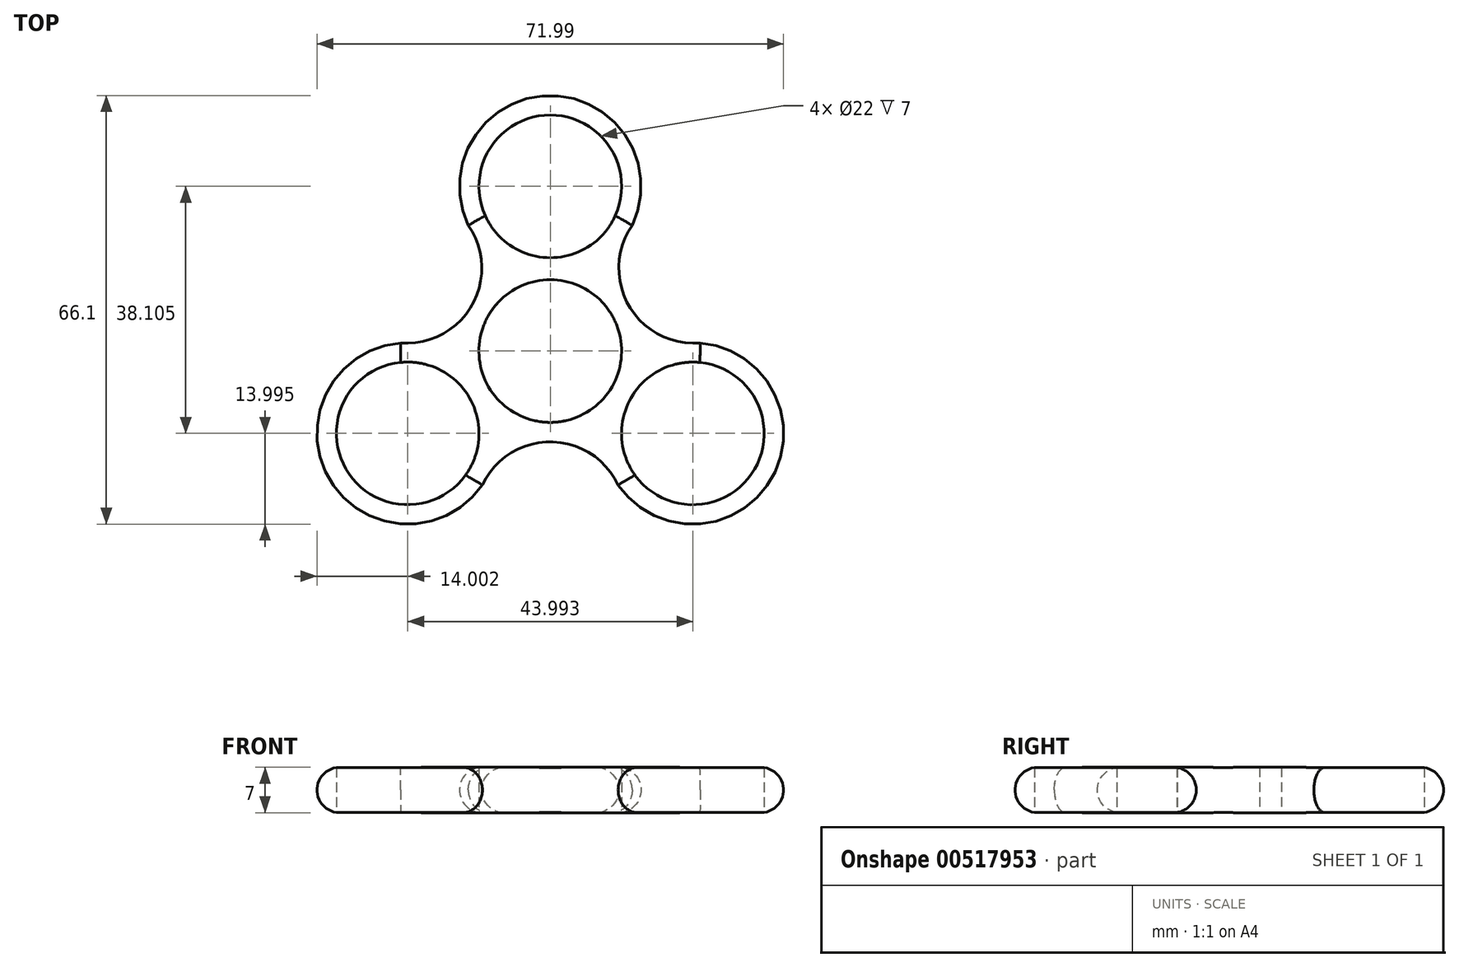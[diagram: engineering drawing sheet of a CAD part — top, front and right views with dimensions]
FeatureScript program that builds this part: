
annotation { "Feature Type Name" : "Feature", "Feature Type Description" : "" }
export const myFeature = defineFeature(function(context is Context, id is Id, definition is map)
    precondition{}
    {
        {
            var Q0;
            Q0=qCreatedBy(makeId("Top.planeOp"),FACE);
            var sketch = newSketch(context, id + "F0", { "sketchPlane" : qUnion([Q0])});
            skCircle(sketch, "E0", {"center": v(0, 0) * mm, "radius": 11 * mm});
            skCircle(sketch, "E1", {"center": v(0, 25.4) * mm, "radius": 11 * mm});
            skArc(sketch, "E2", {"start": v(11.62, 17.59) * mm, "mid": v(0, 39.4) * mm, "end": v(-11.62, 17.59) * mm});
            skCircle(sketch, "E3", {"center": v(22, -12.7) * mm, "radius": 11 * mm});
            skArc(sketch, "E4", {"start": v(9.42, -18.86) * mm, "mid": v(34.12, -19.7) * mm, "end": v(21.04, 1.26) * mm});
            skCircle(sketch, "E5", {"center": v(-22, -12.7) * mm, "radius": 11 * mm});
            skArc(sketch, "E6", {"start": v(-21.04, 1.27) * mm, "mid": v(-34.12, -19.7) * mm, "end": v(-9.42, -18.85) * mm});
            skArc(sketch, "E7", {"start": v(12.65, 19.4) * mm, "mid": v(12.13, 7) * mm, "end": v(23.12, 1.25) * mm});
            skArc(sketch, "E8", {"start": v(-23.12, 1.26) * mm, "mid": v(-12.12, 7) * mm, "end": v(-12.65, 19.4) * mm});
            skArc(sketch, "E9", {"start": v(10.47, -20.65) * mm, "mid": v(0, -14) * mm, "end": v(-10.47, -20.65) * mm});
            skPoint(sketch, "E10.orphan", {"position": v(-5.9, 12.7) * mm});
            skPoint(sketch, "E11.orphan", {"position": v(5.9, 12.7) * mm});
            skPoint(sketch, "E12.trimOffspring.start.orphan", {"position": v(13.94, -1.25) * mm});
            skPoint(sketch, "E13.orphan", {"position": v(8.05, -11.45) * mm});
            skPoint(sketch, "E14.orphan", {"position": v(-8.05, -11.45) * mm});
            skPoint(sketch, "E15.orphan", {"position": v(-13.94, -1.25) * mm});
            skSolve(sketch);
        }
        {
            var Q0;
            Q0=makeQuery(id+"F0.imprint","IMPRINT",FACE,{"disambiguationData":[TD([[makeQuery(id+"F0.imprint","IMPRINT",EDGE,{"derivedFrom":sQuery(id+"F0.wireOp",EDGE,"E0")}),-1.0]])]});
            extrude(context, id + "F1", {"entities" : qUnion([Q0]), "depth" : 7 * mm, "offsetDistance" : 25.4 * mm});
        }
        {
            var Q0;
            Q0=makeQuery(id+"F1.opExtrude","CAP_EDGE",EDGE,{"disambiguationData":[OSD([sQuery(id+"F0.wireOp",EDGE,"E7")])],"isStart":false});
            var Q1;
            Q1=makeQuery(id+"F1.opExtrude","CAP_EDGE",EDGE,{"disambiguationData":[OSD([sQuery(id+"F0.wireOp",EDGE,"E2")])],"isStart":false});
            var Q2;
            Q2=makeQuery(id+"F1.opExtrude","CAP_EDGE",EDGE,{"disambiguationData":[OSD([sQuery(id+"F0.wireOp",EDGE,"E8")])],"isStart":false});
            var Q3;
            Q3=makeQuery(id+"F1.opExtrude","CAP_EDGE",EDGE,{"disambiguationData":[OSD([sQuery(id+"F0.wireOp",EDGE,"E6")])],"isStart":false});
            var Q4;
            Q4=makeQuery(id+"F1.opExtrude","CAP_EDGE",EDGE,{"disambiguationData":[OSD([sQuery(id+"F0.wireOp",EDGE,"E9")])],"isStart":false});
            var Q5;
            Q5=makeQuery(id+"F1.opExtrude","CAP_EDGE",EDGE,{"disambiguationData":[OSD([sQuery(id+"F0.wireOp",EDGE,"E4")])],"isStart":false});
            var Q6;
            Q6=makeQuery(id+"F1.opExtrude","CAP_EDGE",EDGE,{"disambiguationData":[OSD([sQuery(id+"F0.wireOp",EDGE,"E9")])],"isStart":true});
            var Q7;
            Q7=makeQuery(id+"F1.opExtrude","CAP_EDGE",EDGE,{"disambiguationData":[OSD([sQuery(id+"F0.wireOp",EDGE,"E4")])],"isStart":true});
            var Q8;
            Q8=makeQuery(id+"F1.opExtrude","CAP_EDGE",EDGE,{"disambiguationData":[OSD([sQuery(id+"F0.wireOp",EDGE,"E7")])],"isStart":true});
            var Q9;
            Q9=makeQuery(id+"F1.opExtrude","CAP_EDGE",EDGE,{"disambiguationData":[OSD([sQuery(id+"F0.wireOp",EDGE,"E2")])],"isStart":true});
            var Q10;
            Q10=makeQuery(id+"F1.opExtrude","CAP_EDGE",EDGE,{"disambiguationData":[OSD([sQuery(id+"F0.wireOp",EDGE,"E8")])],"isStart":true});
            var Q11;
            Q11=makeQuery(id+"F1.opExtrude","CAP_EDGE",EDGE,{"disambiguationData":[OSD([sQuery(id+"F0.wireOp",EDGE,"E6")])],"isStart":true});
            fillet(context, id + "F2", {"entities" : qUnion([Q0, Q1, Q2, Q3, Q4, Q5, Q6, Q7, Q8, Q9, Q10, Q11]), "radius" : 3.5 * mm, "tangentPropagation" : true, "allowEdgeOverflow" : false});
        }
    });
